# Revit family: Keilhauer-Toob-Table+
name_source: partatom
category: Furniture
units: mm (PartAtom-declared; Revit-internal decimal feet)

## family parameters
Always vertical = Yes
Cut with Voids When Loaded = No
OmniClass Number = 23.40.20.00
OmniClass Title = General Furniture and Specialties
Room Calculation Point = No
Shared = No
Work Plane-Based = No

## types (1)
- 98200
    Assembly Code = E2020200
    Default Elevation = 0"
    Depth = 31 1/2"
    Description = Occasional Table
    Height = 16 3/4"
    Keynote = 12500
    Low Emitting Finish = Yes
    Low Emitting Material = Yes
    Manufacturer = Keilhauer
    Model = 98200
    Percentage of Recycled Content = 0
    Product Documentation Link = https://keilhauer.com
    Revit File Built By = https://servex-us.com
    Salvage or Reuse = Yes
    Type Comments = Toob
    URL = https://keilhauer.com
    Width = 31 1/2"

## geometry (parser evidence)
native form markers: Sweep x5
no freeform markers — native parametric forms only
